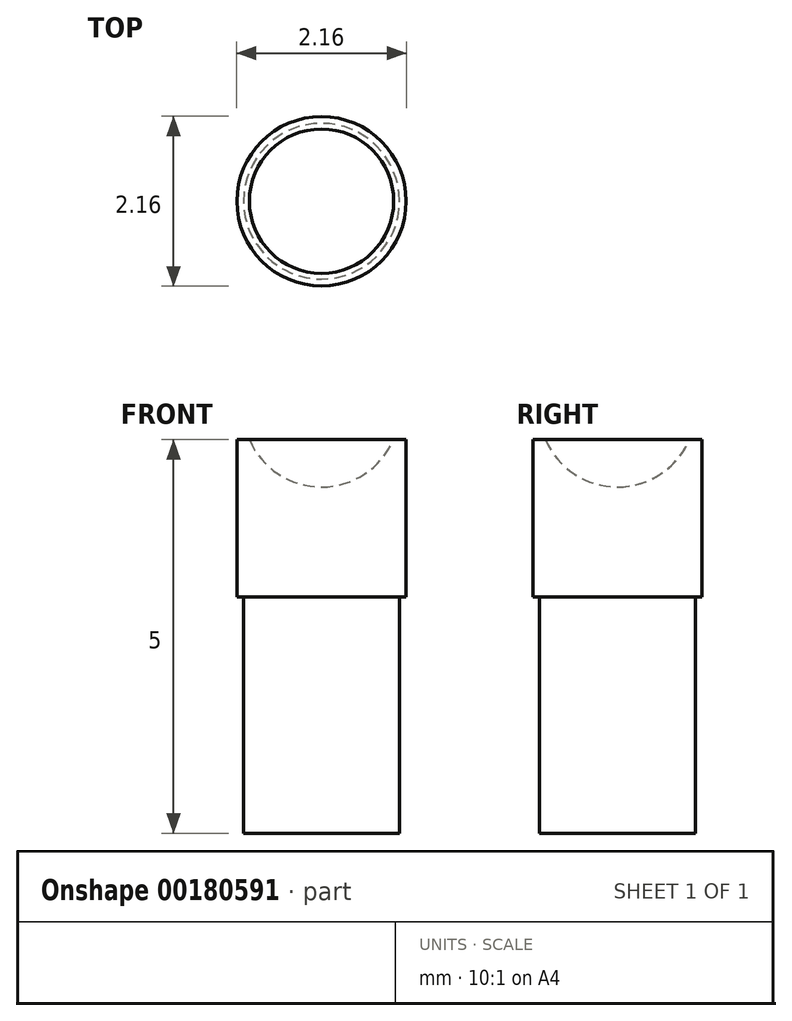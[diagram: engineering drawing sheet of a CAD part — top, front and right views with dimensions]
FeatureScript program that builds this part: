
annotation { "Feature Type Name" : "Feature", "Feature Type Description" : "" }
export const myFeature = defineFeature(function(context is Context, id is Id, definition is map)
    precondition{}
    {
        {
            var Q0;
            Q0=qCreatedBy(makeId("Top.planeOp"),FACE);
            var sketch = newSketch(context, id + "F0", { "sketchPlane" : qUnion([Q0])});
            skCircle(sketch, "E0", {"center": v(0, 0) * mm, "radius": 1.07 * mm});
            skSolve(sketch);
        }
        {
            var Q0;
            Q0 = qSketchRegion(id + "F0", true);
            extrude(context, id + "F1", {"entities" : qUnion([Q0]), "depth" : 2 * mm});
        }
        {
            var Q0;
            Q0=makeQuery(id+"F1.opExtrude","CAP_FACE",FACE,{"disambiguationData":[OSD([sQuery(id+"F0.wireOp",EDGE,"E0")])],"isStart":true});
            var sketch = newSketch(context, id + "F2", { "sketchPlane" : qUnion([Q0])});
            skCircle(sketch, "E1", {"center": v(0, 0) * mm, "radius": 0.99 * mm});
            skSolve(sketch);
        }
        {
            var Q0;
            Q0 = qSketchRegion(id + "F2", true);
            extrude(context, id + "F3", {"entities" : qUnion([Q0]), "operationType" : NewBodyOperationType.ADD, "depth" : 3 * mm});
        }
        {
            var Q0;
            Q0=qCreatedBy(makeId("Right.planeOp"),FACE);
            var sketch = newSketch(context, id + "F4", { "sketchPlane" : qUnion([Q0])});
            skLineSegment(sketch, "E2", {"start": v(0, 0) * mm, "end": v(0, 2.4) * mm, "construction": true});
            skArc(sketch, "E3", {"start": v(0, 3.4) * mm, "mid": v(-1, 2.4) * mm, "end": v(0, 1.4) * mm});
            skLineSegment(sketch, "E4", {"start": v(0, 3.4) * mm, "end": v(0, 1.4) * mm});
            skSolve(sketch);
        }
        {
            var Q0;
            Q0=makeQuery(id+"F4.imprint","IMPRINT",FACE,{"disambiguationData":[TD([[makeQuery(id+"F4.imprint","IMPRINT",EDGE,{"derivedFrom":sQuery(id+"F4.wireOp",EDGE,"E3")}),1.0]])]});
            var Q1;
            Q1=sQuery(id+"F4.wireOp",EDGE,"E2");
            revolve(context, id + "F5", {"operationType" : NewBodyOperationType.REMOVE, "entities" : qUnion([Q0]), "axis" : qUnion([Q1]), "revolveType" : RevolveType.FULL, "oppositeDirection" : true});
        }
    });
